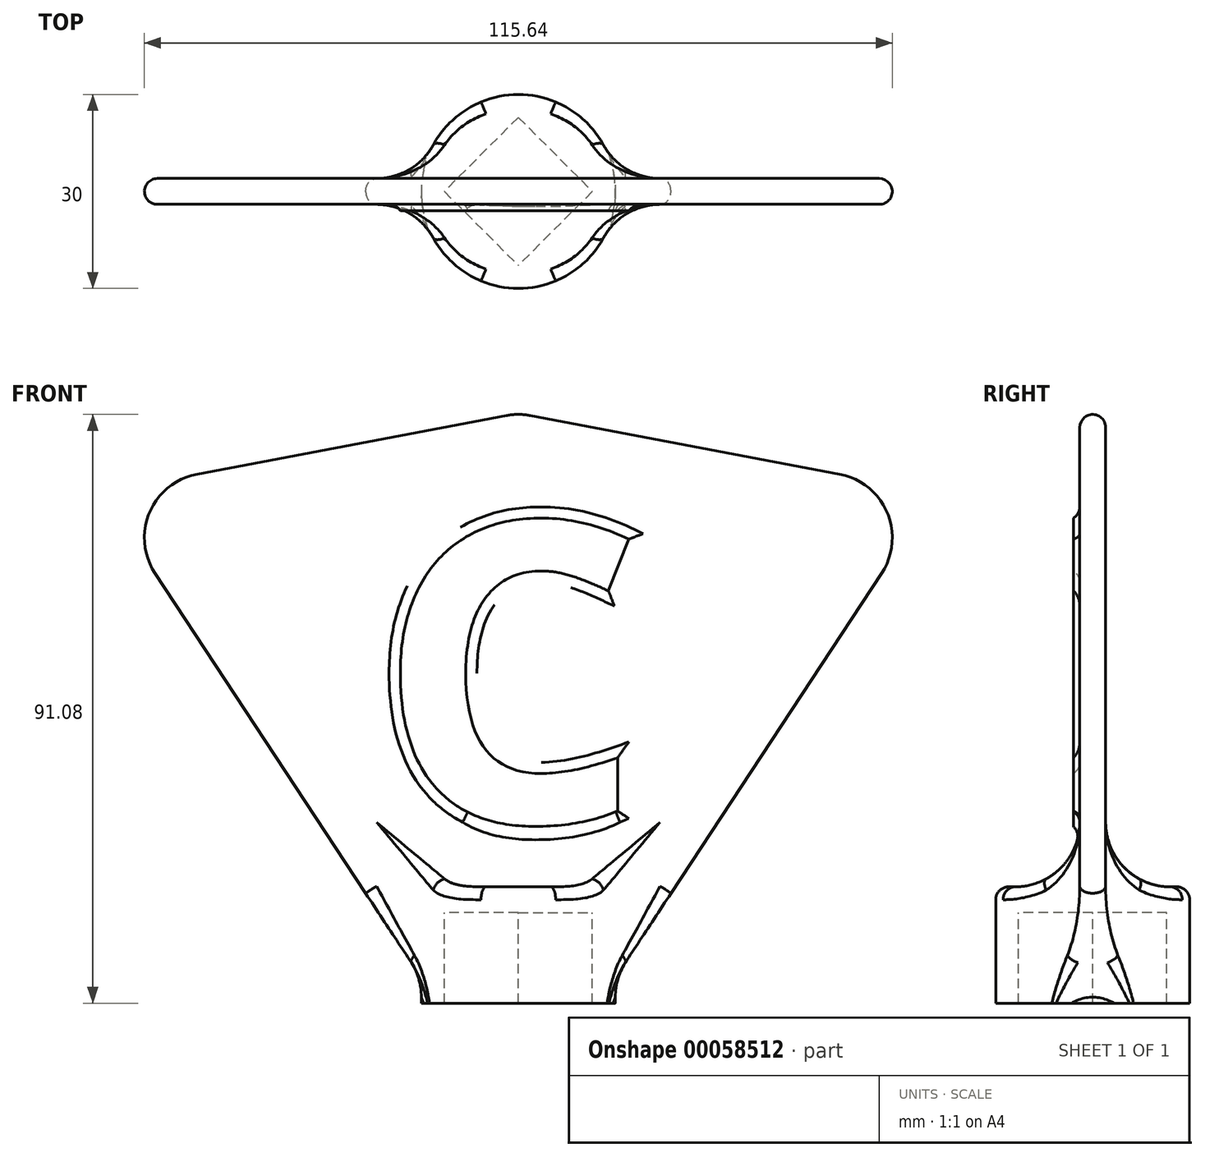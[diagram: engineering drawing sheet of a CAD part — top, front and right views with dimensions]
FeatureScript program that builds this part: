
annotation { "Feature Type Name" : "Feature", "Feature Type Description" : "" }
export const myFeature = defineFeature(function(context is Context, id is Id, definition is map)
    precondition{}
    {
        {
            var Q0;
            Q0=qCreatedBy(makeId("Top.planeOp"),FACE);
            var sketch = newSketch(context, id + "F0", { "sketchPlane" : qUnion([Q0])});
            skLineSegment(sketch, "E0.rect.bottom", {"start": v(0, 11.46) * mm, "end": v(-11.46, 0) * mm});
            skLineSegment(sketch, "E0.rect.top", {"start": v(11.46, 0) * mm, "end": v(0, -11.46) * mm});
            skLineSegment(sketch, "E0.rect.left", {"start": v(0, 11.46) * mm, "end": v(11.46, 0) * mm});
            skLineSegment(sketch, "E0.rect.right", {"start": v(-11.46, 0) * mm, "end": v(0, -11.46) * mm});
            skPoint(sketch, "E0.rect.middle", {"position": v(0, 0) * mm});
            skCircle(sketch, "E1", {"center": v(0, 0) * mm, "radius": 15 * mm});
            skSolve(sketch);
        }
        {
            var Q0;
            Q0 = qSketchRegion(id + "F0", true);
            extrude(context, id + "F1", {"entities" : qUnion([Q0]), "oppositeDirection" : true, "depth" : 14 * mm});
        }
        {
            var Q0;
            Q0=makeQuery(id+"F0.imprint","IMPRINT",FACE,{"disambiguationData":[TD([[makeQuery(id+"F0.imprint","IMPRINT",EDGE,{"derivedFrom":sQuery(id+"F0.wireOp",EDGE,"E0.rect.bottom")}),1.0]])]});
            var Q1;
            Q1=makeQuery(id+"F0.imprint","IMPRINT",FACE,{"disambiguationData":[TD([[makeQuery(id+"F0.imprint","IMPRINT",EDGE,{"derivedFrom":sQuery(id+"F0.wireOp",EDGE,"E0.rect.bottom")}),-1.0]])]});
            extrude(context, id + "F2", {"entities" : qUnion([Q0, Q1]), "operationType" : NewBodyOperationType.ADD, "depth" : 4 * mm});
        }
        {
            var Q0;
            Q0=qCreatedBy(makeId("Front.planeOp"),FACE);
            var sketch = newSketch(context, id + "F3", { "sketchPlane" : qUnion([Q0])});
            skLineSegment(sketch, "E2", {"start": v(-13.5, -12.36) * mm, "end": v(-64.42, 65.03) * mm});
            skLineSegment(sketch, "E3", {"start": v(-64.42, 65.03) * mm, "end": v(0, 77.26) * mm});
            skLineSegment(sketch, "E4", {"start": v(-13.5, -12.36) * mm, "end": v(-13.5, 2.03) * mm});
            skLineSegment(sketch, "E5", {"start": v(-13.5, 2.03) * mm, "end": v(0, 2.03) * mm});
            skLineSegment(sketch, "E6.MirrorCS", {"start": v(64.42, 65.03) * mm, "end": v(0, 77.26) * mm});
            skLineSegment(sketch, "E7.MirrorCS", {"start": v(13.5, 2.03) * mm, "end": v(0, 2.03) * mm});
            skLineSegment(sketch, "E8.MirrorCS", {"start": v(13.5, -12.36) * mm, "end": v(64.42, 65.03) * mm});
            skLineSegment(sketch, "E9.MirrorCS", {"start": v(13.5, -12.36) * mm, "end": v(13.5, 2.03) * mm});
            skSolve(sketch);
        }
        {
            var Q0;
            Q0 = qSketchRegion(id + "F3", true);
            extrude(context, id + "F4", {"entities" : qUnion([Q0]), "operationType" : NewBodyOperationType.ADD, "endBound" : BoundingType.SYMMETRIC, "depth" : 4 * mm});
        }
        {
            var Q0;
            Q0=makeQuery(id+"F4.opExtrude","CAP_FACE",FACE,{"disambiguationData":[OSD([sQuery(id+"F3.wireOp",EDGE,"E2"),sQuery(id+"F3.wireOp",EDGE,"E3"),sQuery(id+"F3.wireOp",EDGE,"E4"),sQuery(id+"F3.wireOp",EDGE,"E5"),sQuery(id+"F3.wireOp",EDGE,"E6.MirrorCS"),sQuery(id+"F3.wireOp",EDGE,"E7.MirrorCS"),sQuery(id+"F3.wireOp",EDGE,"E8.MirrorCS"),sQuery(id+"F3.wireOp",EDGE,"E9.MirrorCS")])],"isStart":false});
            var sketch = newSketch(context, id + "F5", { "sketchPlane" : qUnion([Q0])});
            skText(sketch, "E10", { "text": "C", "fontName": "OpenSans-Bold.ttf"});
            const initialGuessF5  = {"E10": [-0.02203, 0.01398, 1, 0, 0.0468]};
            skSetInitialGuess(sketch, initialGuessF5);
            skSolve(sketch);
        }
        {
            var Q0;
            Q0=makeQuery(id+"F5.imprint","IMPRINT",FACE,{"disambiguationData":[TD([[makeQuery(id+"F5.imprint","IMPRINT",EDGE,{"derivedFrom":sQuery(id+"F5.wireOp",EDGE,"E10.sketch_text.stroke-0")}),-1.0]])]});
            extrude(context, id + "F6", {"entities" : qUnion([Q0]), "operationType" : NewBodyOperationType.ADD, "depth" : 1 * mm});
        }
        {
            var Q0;
            Q0=makeQuery(id+"F4.boolean.opBoolean","INTERSECT",EDGE,{"derivedFrom":[makeQuery(id+"F2.opExtrude","CAP_FACE",FACE,{"disambiguationData":[OSD([sQuery(id+"F0.wireOp",EDGE,"E1")])],"isStart":false}),makeQuery(id+"F4.opExtrude","CAP_FACE",FACE,{"disambiguationData":[OSD([sQuery(id+"F3.wireOp",EDGE,"E2"),sQuery(id+"F3.wireOp",EDGE,"E3"),sQuery(id+"F3.wireOp",EDGE,"E4"),sQuery(id+"F3.wireOp",EDGE,"E5"),sQuery(id+"F3.wireOp",EDGE,"E6.MirrorCS"),sQuery(id+"F3.wireOp",EDGE,"E7.MirrorCS"),sQuery(id+"F3.wireOp",EDGE,"E8.MirrorCS"),sQuery(id+"F3.wireOp",EDGE,"E9.MirrorCS")])],"isStart":false})]});
            var Q1;
            Q1=makeQuery(id+"F4.boolean.opBoolean","INTERSECT",EDGE,{"derivedFrom":[makeQuery(id+"F2.opExtrude","CAP_FACE",FACE,{"disambiguationData":[OSD([sQuery(id+"F0.wireOp",EDGE,"E1")])],"isStart":false}),makeQuery(id+"F4.opExtrude","CAP_FACE",FACE,{"disambiguationData":[OSD([sQuery(id+"F3.wireOp",EDGE,"E2"),sQuery(id+"F3.wireOp",EDGE,"E3"),sQuery(id+"F3.wireOp",EDGE,"E4"),sQuery(id+"F3.wireOp",EDGE,"E5"),sQuery(id+"F3.wireOp",EDGE,"E6.MirrorCS"),sQuery(id+"F3.wireOp",EDGE,"E7.MirrorCS"),sQuery(id+"F3.wireOp",EDGE,"E8.MirrorCS"),sQuery(id+"F3.wireOp",EDGE,"E9.MirrorCS")])],"isStart":true})]});
            var Q2;
            {var subQ0=sQuery(id+"F0.wireOp",EDGE,"E1");Q2=makeQuery(id+"F4.boolean.opBoolean","INTERSECT",EDGE,{"disambiguationData":[OD(1.0)],"derivedFrom":[makeQuery(id+"F2.boolean.opBoolean","MERGE",FACE,{"derivedFrom":[makeQuery(id+"F1.opExtrude","SWEPT_FACE",FACE,{"disambiguationData":[OSD([subQ0])]}),makeQuery(id+"F2.opExtrude","SWEPT_FACE",FACE,{"disambiguationData":[OSD([subQ0])]})]}),makeQuery(id+"F4.opExtrude","CAP_FACE",FACE,{"disambiguationData":[OSD([sQuery(id+"F3.wireOp",EDGE,"E2"),sQuery(id+"F3.wireOp",EDGE,"E3"),sQuery(id+"F3.wireOp",EDGE,"E4"),sQuery(id+"F3.wireOp",EDGE,"E5"),sQuery(id+"F3.wireOp",EDGE,"E6.MirrorCS"),sQuery(id+"F3.wireOp",EDGE,"E7.MirrorCS"),sQuery(id+"F3.wireOp",EDGE,"E8.MirrorCS"),sQuery(id+"F3.wireOp",EDGE,"E9.MirrorCS")])],"isStart":false})]});}
            var Q3;
            {var subQ0=sQuery(id+"F0.wireOp",EDGE,"E1");Q3=makeQuery(id+"F4.boolean.opBoolean","INTERSECT",EDGE,{"disambiguationData":[OD(1.0)],"derivedFrom":[makeQuery(id+"F2.boolean.opBoolean","MERGE",FACE,{"derivedFrom":[makeQuery(id+"F1.opExtrude","SWEPT_FACE",FACE,{"disambiguationData":[OSD([subQ0])]}),makeQuery(id+"F2.opExtrude","SWEPT_FACE",FACE,{"disambiguationData":[OSD([subQ0])]})]}),makeQuery(id+"F4.opExtrude","CAP_FACE",FACE,{"disambiguationData":[OSD([sQuery(id+"F3.wireOp",EDGE,"E2"),sQuery(id+"F3.wireOp",EDGE,"E3"),sQuery(id+"F3.wireOp",EDGE,"E4"),sQuery(id+"F3.wireOp",EDGE,"E5"),sQuery(id+"F3.wireOp",EDGE,"E6.MirrorCS"),sQuery(id+"F3.wireOp",EDGE,"E7.MirrorCS"),sQuery(id+"F3.wireOp",EDGE,"E8.MirrorCS"),sQuery(id+"F3.wireOp",EDGE,"E9.MirrorCS")])],"isStart":true})]});}
            var Q4;
            {var subQ0=sQuery(id+"F0.wireOp",EDGE,"E1");Q4=makeQuery(id+"F4.boolean.opBoolean","INTERSECT",EDGE,{"disambiguationData":[OD(0.0)],"derivedFrom":[makeQuery(id+"F2.boolean.opBoolean","MERGE",FACE,{"derivedFrom":[makeQuery(id+"F1.opExtrude","SWEPT_FACE",FACE,{"disambiguationData":[OSD([subQ0])]}),makeQuery(id+"F2.opExtrude","SWEPT_FACE",FACE,{"disambiguationData":[OSD([subQ0])]})]}),makeQuery(id+"F4.opExtrude","CAP_FACE",FACE,{"disambiguationData":[OSD([sQuery(id+"F3.wireOp",EDGE,"E2"),sQuery(id+"F3.wireOp",EDGE,"E3"),sQuery(id+"F3.wireOp",EDGE,"E4"),sQuery(id+"F3.wireOp",EDGE,"E5"),sQuery(id+"F3.wireOp",EDGE,"E6.MirrorCS"),sQuery(id+"F3.wireOp",EDGE,"E7.MirrorCS"),sQuery(id+"F3.wireOp",EDGE,"E8.MirrorCS"),sQuery(id+"F3.wireOp",EDGE,"E9.MirrorCS")])],"isStart":true})]});}
            var Q5;
            {var subQ0=sQuery(id+"F0.wireOp",EDGE,"E1");Q5=makeQuery(id+"F4.boolean.opBoolean","INTERSECT",EDGE,{"disambiguationData":[OD(0.0)],"derivedFrom":[makeQuery(id+"F2.boolean.opBoolean","MERGE",FACE,{"derivedFrom":[makeQuery(id+"F1.opExtrude","SWEPT_FACE",FACE,{"disambiguationData":[OSD([subQ0])]}),makeQuery(id+"F2.opExtrude","SWEPT_FACE",FACE,{"disambiguationData":[OSD([subQ0])]})]}),makeQuery(id+"F4.opExtrude","CAP_FACE",FACE,{"disambiguationData":[OSD([sQuery(id+"F3.wireOp",EDGE,"E2"),sQuery(id+"F3.wireOp",EDGE,"E3"),sQuery(id+"F3.wireOp",EDGE,"E4"),sQuery(id+"F3.wireOp",EDGE,"E5"),sQuery(id+"F3.wireOp",EDGE,"E6.MirrorCS"),sQuery(id+"F3.wireOp",EDGE,"E7.MirrorCS"),sQuery(id+"F3.wireOp",EDGE,"E8.MirrorCS"),sQuery(id+"F3.wireOp",EDGE,"E9.MirrorCS")])],"isStart":false})]});}
            var Q6;
            {var subQ0=sQuery(id+"F0.wireOp",EDGE,"E1");Q6=makeQuery(id+"F4.boolean.opBoolean","INTERSECT",EDGE,{"derivedFrom":[makeQuery(id+"F2.boolean.opBoolean","MERGE",FACE,{"derivedFrom":[makeQuery(id+"F1.opExtrude","SWEPT_FACE",FACE,{"disambiguationData":[OSD([subQ0])]}),makeQuery(id+"F2.opExtrude","SWEPT_FACE",FACE,{"disambiguationData":[OSD([subQ0])]})]}),makeQuery(id+"F4.opExtrude","SWEPT_FACE",FACE,{"disambiguationData":[OSD([sQuery(id+"F3.wireOp",EDGE,"E2")])]})]});}
            var Q7;
            {var subQ0=sQuery(id+"F0.wireOp",EDGE,"E1");Q7=makeQuery(id+"F4.boolean.opBoolean","INTERSECT",EDGE,{"derivedFrom":[makeQuery(id+"F2.boolean.opBoolean","MERGE",FACE,{"derivedFrom":[makeQuery(id+"F1.opExtrude","SWEPT_FACE",FACE,{"disambiguationData":[OSD([subQ0])]}),makeQuery(id+"F2.opExtrude","SWEPT_FACE",FACE,{"disambiguationData":[OSD([subQ0])]})]}),makeQuery(id+"F4.opExtrude","SWEPT_FACE",FACE,{"disambiguationData":[OSD([sQuery(id+"F3.wireOp",EDGE,"E8.MirrorCS")])]})]});}
            var Q8;
            Q8=makeQuery(id+"F4.opExtrude","SWEPT_EDGE",EDGE,{"disambiguationData":[OSD([sQuery(id+"F3.wireOp",EDGE,"E6.MirrorCS"),sQuery(id+"F3.wireOp",EDGE,"E8.MirrorCS")])]});
            var Q9;
            Q9=makeQuery(id+"F4.opExtrude","SWEPT_EDGE",EDGE,{"disambiguationData":[OSD([sQuery(id+"F3.wireOp",EDGE,"E2"),sQuery(id+"F3.wireOp",EDGE,"E3")])]});
            var Q10;
            Q10=makeQuery(id+"F4.opExtrude","SWEPT_EDGE",EDGE,{"disambiguationData":[OSD([sQuery(id+"F3.wireOp",EDGE,"E3"),sQuery(id+"F3.wireOp",EDGE,"E6.MirrorCS")])]});
            fillet(context, id + "F7", {"entities" : qUnion([Q0, Q1, Q2, Q3, Q4, Q5, Q6, Q7, Q8, Q9, Q10]), "radius" : 10 * mm, "tangentPropagation" : true, "allowEdgeOverflow" : false});
        }
        {
            var Q0;
            Q0=makeQuery(id+"F4.opExtrude","CAP_EDGE",EDGE,{"disambiguationData":[OSD([sQuery(id+"F3.wireOp",EDGE,"E8.MirrorCS")])],"isStart":false});
            var Q1;
            {var subQ0=sQuery(id+"F3.wireOp",EDGE,"E8.MirrorCS");var subQ1=sQuery(id+"F3.wireOp",EDGE,"E6.MirrorCS");Q1=makeQuery(id+"F7.opFillet","BLEND_EDGE",EDGE,{"blendedFrom":[makeQuery(id+"F4.opExtrude","SWEPT_EDGE",EDGE,{"disambiguationData":[OSD([subQ1,subQ0])]}),makeQuery(id+"F4.opExtrude","CAP_FACE",FACE,{"disambiguationData":[OSD([sQuery(id+"F3.wireOp",EDGE,"E2"),sQuery(id+"F3.wireOp",EDGE,"E3"),sQuery(id+"F3.wireOp",EDGE,"E4"),sQuery(id+"F3.wireOp",EDGE,"E5"),subQ1,sQuery(id+"F3.wireOp",EDGE,"E7.MirrorCS"),subQ0,sQuery(id+"F3.wireOp",EDGE,"E9.MirrorCS")])],"isStart":true})],"blendedInto":[makeQuery(id+"F4.opExtrude","CAP_FACE",FACE,{"disambiguationData":[OSD([sQuery(id+"F3.wireOp",EDGE,"E2"),sQuery(id+"F3.wireOp",EDGE,"E3"),sQuery(id+"F3.wireOp",EDGE,"E4"),sQuery(id+"F3.wireOp",EDGE,"E5"),subQ1,sQuery(id+"F3.wireOp",EDGE,"E7.MirrorCS"),subQ0,sQuery(id+"F3.wireOp",EDGE,"E9.MirrorCS")])],"isStart":true})]});}
            var Q2;
            {var subQ0=sQuery(id+"F0.wireOp",EDGE,"E1");Q2=makeQuery(id+"F4.boolean.opBoolean","SPLIT",EDGE,{"disambiguationData":[TD([makeQuery(id+"F4.opExtrude","CAP_FACE",FACE,{"disambiguationData":[OSD([sQuery(id+"F3.wireOp",EDGE,"E2"),sQuery(id+"F3.wireOp",EDGE,"E3"),sQuery(id+"F3.wireOp",EDGE,"E4"),sQuery(id+"F3.wireOp",EDGE,"E5"),sQuery(id+"F3.wireOp",EDGE,"E6.MirrorCS"),sQuery(id+"F3.wireOp",EDGE,"E7.MirrorCS"),sQuery(id+"F3.wireOp",EDGE,"E8.MirrorCS"),sQuery(id+"F3.wireOp",EDGE,"E9.MirrorCS")])],"isStart":true})])],"derivedFrom":makeQuery(id+"F2.opExtrude","CAP_EDGE",EDGE,{"disambiguationData":[OSD([subQ0])],"isStart":false})});}
            var Q3;
            {var subQ0=sQuery(id+"F0.wireOp",EDGE,"E1");Q3=makeQuery(id+"F4.boolean.opBoolean","SPLIT",EDGE,{"disambiguationData":[TD([makeQuery(id+"F4.opExtrude","CAP_FACE",FACE,{"disambiguationData":[OSD([sQuery(id+"F3.wireOp",EDGE,"E2"),sQuery(id+"F3.wireOp",EDGE,"E3"),sQuery(id+"F3.wireOp",EDGE,"E4"),sQuery(id+"F3.wireOp",EDGE,"E5"),sQuery(id+"F3.wireOp",EDGE,"E6.MirrorCS"),sQuery(id+"F3.wireOp",EDGE,"E7.MirrorCS"),sQuery(id+"F3.wireOp",EDGE,"E8.MirrorCS"),sQuery(id+"F3.wireOp",EDGE,"E9.MirrorCS")])],"isStart":false})])],"derivedFrom":makeQuery(id+"F2.opExtrude","CAP_EDGE",EDGE,{"disambiguationData":[OSD([subQ0])],"isStart":false})});}
            var Q4;
            Q4=makeQuery(id+"F4.opExtrude","CAP_FACE",FACE,{"disambiguationData":[OSD([sQuery(id+"F3.wireOp",EDGE,"E2"),sQuery(id+"F3.wireOp",EDGE,"E3"),sQuery(id+"F3.wireOp",EDGE,"E4"),sQuery(id+"F3.wireOp",EDGE,"E5"),sQuery(id+"F3.wireOp",EDGE,"E6.MirrorCS"),sQuery(id+"F3.wireOp",EDGE,"E7.MirrorCS"),sQuery(id+"F3.wireOp",EDGE,"E8.MirrorCS"),sQuery(id+"F3.wireOp",EDGE,"E9.MirrorCS")])],"isStart":false});
            fillet(context, id + "F8", {"entities" : qUnion([Q0, Q1, Q2, Q3, Q4]), "radius" : 2 * mm, "tangentPropagation" : true, "allowEdgeOverflow" : false});
        }
    });
